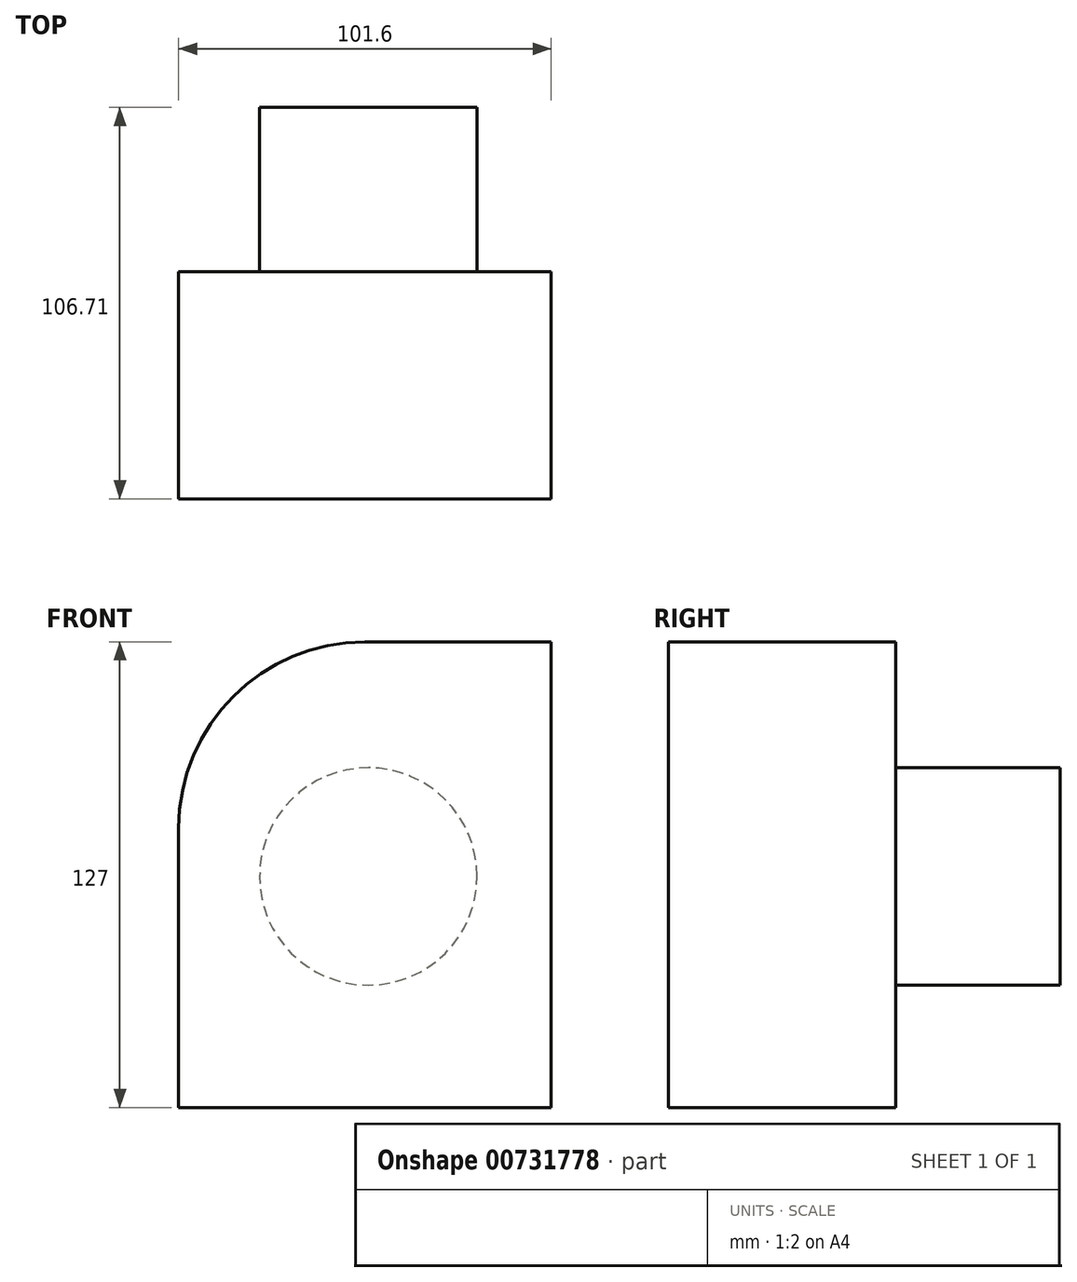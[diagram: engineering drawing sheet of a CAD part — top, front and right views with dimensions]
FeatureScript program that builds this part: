
annotation { "Feature Type Name" : "Feature", "Feature Type Description" : "" }
export const myFeature = defineFeature(function(context is Context, id is Id, definition is map)
    precondition{}
    {
        {
            var Q0;
            Q0=qCreatedBy(makeId("Front.planeOp"),FACE);
            var sketch = newSketch(context, id + "F0", { "sketchPlane" : qUnion([Q0])});
            skLineSegment(sketch, "E0.bottom", {"start": v(35.66, 104.35) * mm, "end": v(86.46, 104.35) * mm});
            skLineSegment(sketch, "E0.top", {"start": v(-15.14, -22.65) * mm, "end": v(86.46, -22.65) * mm});
            skLineSegment(sketch, "E0.left", {"start": v(-15.14, 53.55) * mm, "end": v(-15.14, -22.65) * mm});
            skLineSegment(sketch, "E0.right", {"start": v(86.46, 104.35) * mm, "end": v(86.46, -22.65) * mm});
            skPoint(sketch, "E1.visualSharp", {"position": v(-15.14, 104.35) * mm});
            skArc(sketch, "E1.filletArc", {"start": v(35.66, 104.35) * mm, "mid": v(-0.26, 89.47) * mm, "end": v(-15.14, 53.55) * mm});
            skSolve(sketch);
        }
        {
            var Q0;
            Q0 = qSketchRegion(id + "F0", true);
            var Q1;
            Q1 = qBodyType(qCreatedBy(id + "F0" ,EDGE), BodyType.WIRE);
            extrude(context, id + "F1", {"entities" : qUnion([Q0]), "surfaceEntities" : qUnion([Q1]), "depth" : 61.94 * mm, "offsetDistance" : 25.4 * mm});
        }
        {
            var Q0;
            Q0=makeQuery(id+"F1.opExtrude","CAP_FACE",FACE,{"disambiguationData":[OSD([sQuery(id+"F0.wireOp",EDGE,"E0.bottom"),sQuery(id+"F0.wireOp",EDGE,"E0.top"),sQuery(id+"F0.wireOp",EDGE,"E0.left"),sQuery(id+"F0.wireOp",EDGE,"E0.right"),sQuery(id+"F0.wireOp",EDGE,"E1.filletArc")])],"isStart":true});
            var sketch = newSketch(context, id + "F2", { "sketchPlane" : qUnion([Q0])});
            skCircle(sketch, "E2", {"center": v(-36.57, 40.35) * mm, "radius": 29.64 * mm});
            skSolve(sketch);
        }
        {
            var Q0;
            Q0=makeQuery(id+"F2.imprint","IMPRINT",FACE,{"disambiguationData":[TD([[makeQuery(id+"F2.imprint","IMPRINT",EDGE,{"derivedFrom":sQuery(id+"F2.wireOp",EDGE,"E2")}),1.0]])]});
            extrude(context, id + "F3", {"entities" : qUnion([Q0]), "operationType" : NewBodyOperationType.ADD, "depth" : 44.77 * mm, "offsetDistance" : 25 * mm});
        }
    });
